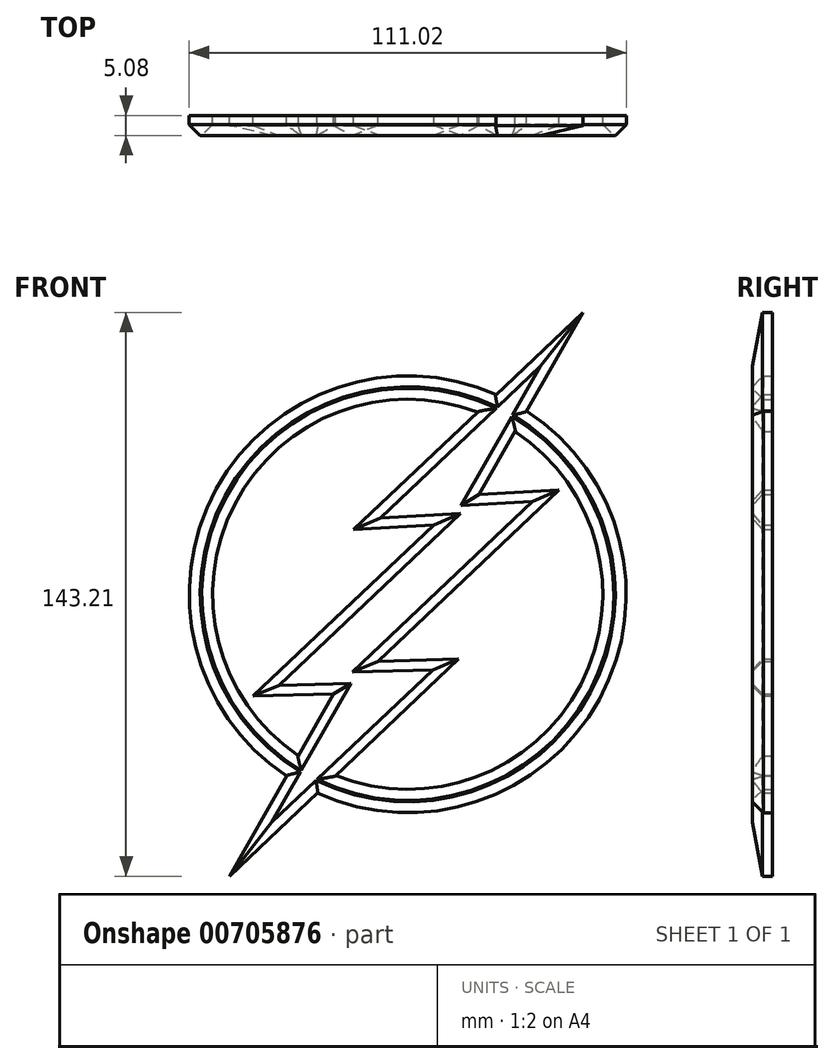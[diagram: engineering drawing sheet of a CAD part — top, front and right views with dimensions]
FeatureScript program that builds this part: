
annotation { "Feature Type Name" : "Feature", "Feature Type Description" : "" }
export const myFeature = defineFeature(function(context is Context, id is Id, definition is map)
    precondition{}
    {
        {
            var Q0;
            Q0=qCreatedBy(makeId("Front.planeOp"),FACE);
            var sketch = newSketch(context, id + "F0", { "sketchPlane" : qUnion([Q0])});
            skLineSegment(sketch, "E0", {"start": v(44.49, 71.6) * mm, "end": v(-13.73, 16.46) * mm});
            skLineSegment(sketch, "E1", {"start": v(38.43, 26.46) * mm, "end": v(18.04, 25.32) * mm});
            skLineSegment(sketch, "E2", {"start": v(18.04, 25.32) * mm, "end": v(44.49, 71.6) * mm});
            skLineSegment(sketch, "E3.MirrorCS", {"start": v(-45.3, -71.61) * mm, "end": v(12.92, -16.48) * mm});
            skLineSegment(sketch, "E4.MirrorCS", {"start": v(-39.27, -25.89) * mm, "end": v(-18.85, -25.33) * mm});
            skLineSegment(sketch, "E5", {"start": v(-18.85, -25.33) * mm, "end": v(-45.3, -71.61) * mm});
            skLineSegment(sketch, "E6", {"start": v(6.66, 17.61) * mm, "end": v(-39.27, -25.89) * mm});
            skLineSegment(sketch, "E7", {"start": v(-7.5, -17.03) * mm, "end": v(38.43, 26.46) * mm});
            skLineSegment(sketch, "E8", {"start": v(6.66, 17.61) * mm, "end": v(-13.73, 16.46) * mm});
            skLineSegment(sketch, "E9", {"start": v(12.92, -16.48) * mm, "end": v(-7.5, -17.03) * mm});
            skSolve(sketch);
        }
        {
            var Q0;
            Q0=qCreatedBy(makeId("Front.planeOp"),FACE);
            var sketch = newSketch(context, id + "F1", { "sketchPlane" : qUnion([Q0])});
            skCircle(sketch, "E10", {"center": v(0, 0) * mm, "radius": 55.5 * mm});
            skCircle(sketch, "E11", {"center": v(0, 0) * mm, "radius": 49.55 * mm});
            skSolve(sketch);
        }
        {
            var Q0;
            Q0=makeQuery(id+"F1.imprint","IMPRINT",FACE,{"disambiguationData":[TD([[makeQuery(id+"F1.imprint","IMPRINT",EDGE,{"derivedFrom":sQuery(id+"F1.wireOp",EDGE,"E10")}),1.0]])]});
            extrude(context, id + "F2", {"entities" : qUnion([Q0]), "depth" : 3.56 * mm, "offsetDistance" : 25.4 * mm});
        }
        {
            var Q0;
            Q0=makeQuery(id+"F2.opExtrude","CAP_EDGE",EDGE,{"disambiguationData":[OSD([sQuery(id+"F1.wireOp",EDGE,"E10")])],"isStart":false});
            var Q1;
            Q1=makeQuery(id+"F2.opExtrude","CAP_EDGE",EDGE,{"disambiguationData":[OSD([sQuery(id+"F1.wireOp",EDGE,"E11")])],"isStart":false});
            chamfer(context, id + "F3", {"entities" : qUnion([Q0, Q1]), "width" : 2.8 * mm, "tangentPropagation" : true});
        }
        {
            var Q0;
            Q0 = qSketchRegion(id + "F0", true);
            var Q1;
            Q1 = qSketchRegion(id + "F1", true);
            extrude(context, id + "F4", {"entities" : qUnion([Q0, Q1]), "operationType" : NewBodyOperationType.ADD, "depth" : 5.08 * mm, "offsetDistance" : 25.4 * mm});
        }
        {
            var Q0;
            Q0=makeQuery(id+"F4.opExtrude","CAP_EDGE",EDGE,{"disambiguationData":[OSD([sQuery(id+"F0.wireOp",EDGE,"E0")])],"isStart":false});
            var Q1;
            Q1=makeQuery(id+"F4.opExtrude","CAP_EDGE",EDGE,{"disambiguationData":[OSD([sQuery(id+"F0.wireOp",EDGE,"E2")])],"isStart":false});
            var Q2;
            Q2=makeQuery(id+"F4.opExtrude","CAP_EDGE",EDGE,{"disambiguationData":[OSD([sQuery(id+"F0.wireOp",EDGE,"E8")])],"isStart":false});
            var Q3;
            Q3=makeQuery(id+"F4.opExtrude","CAP_EDGE",EDGE,{"disambiguationData":[OSD([sQuery(id+"F0.wireOp",EDGE,"E6")])],"isStart":false});
            var Q4;
            Q4=makeQuery(id+"F4.opExtrude","CAP_EDGE",EDGE,{"disambiguationData":[OSD([sQuery(id+"F0.wireOp",EDGE,"E7")])],"isStart":false});
            var Q5;
            Q5=makeQuery(id+"F4.opExtrude","CAP_EDGE",EDGE,{"disambiguationData":[OSD([sQuery(id+"F0.wireOp",EDGE,"E1")])],"isStart":false});
            var Q6;
            Q6=makeQuery(id+"F4.opExtrude","CAP_EDGE",EDGE,{"disambiguationData":[OSD([sQuery(id+"F0.wireOp",EDGE,"E9")])],"isStart":false});
            var Q7;
            Q7=makeQuery(id+"F4.opExtrude","CAP_EDGE",EDGE,{"disambiguationData":[OSD([sQuery(id+"F0.wireOp",EDGE,"E4.MirrorCS")])],"isStart":false});
            var Q8;
            Q8=makeQuery(id+"F4.opExtrude","CAP_EDGE",EDGE,{"disambiguationData":[OSD([sQuery(id+"F0.wireOp",EDGE,"E3.MirrorCS")])],"isStart":false});
            var Q9;
            Q9=makeQuery(id+"F4.opExtrude","CAP_EDGE",EDGE,{"disambiguationData":[OSD([sQuery(id+"F0.wireOp",EDGE,"E5")])],"isStart":false});
            chamfer(context, id + "F5", {"entities" : qUnion([Q0, Q1, Q2, Q3, Q4, Q5, Q6, Q7, Q8, Q9]), "width" : 2.54 * mm, "tangentPropagation" : true});
        }
        {
            var Q0;
            {var subQ1=sQuery(id+"F0.wireOp",EDGE,"E0");var subQ2=sQuery(id+"F1.wireOp",EDGE,"E10");Q0=makeQuery(id+"F4.boolean.opBoolean","SPLIT",EDGE,{"disambiguationData":[TD([makeQuery(id+"F4.opExtrude","SWEPT_FACE",FACE,{"disambiguationData":[OSD([subQ1])]})])],"derivedFrom":makeQuery(id+"F4.opExtrude","CAP_EDGE",EDGE,{"disambiguationData":[OSD([subQ2])],"isStart":false})});}
            var Q1;
            {var subQ1=sQuery(id+"F0.wireOp",EDGE,"E0");var subQ2=sQuery(id+"F1.wireOp",EDGE,"E11");Q1=makeQuery(id+"F4.boolean.opBoolean","SPLIT",EDGE,{"disambiguationData":[TD([makeQuery(id+"F4.opExtrude","SWEPT_FACE",FACE,{"disambiguationData":[OSD([subQ1])]})])],"derivedFrom":makeQuery(id+"F4.opExtrude","CAP_EDGE",EDGE,{"disambiguationData":[OSD([subQ2])],"isStart":false})});}
            var Q2;
            {var subQ1=sQuery(id+"F0.wireOp",EDGE,"E2");var subQ2=sQuery(id+"F1.wireOp",EDGE,"E11");Q2=makeQuery(id+"F4.boolean.opBoolean","SPLIT",EDGE,{"disambiguationData":[TD([makeQuery(id+"F4.opExtrude","SWEPT_FACE",FACE,{"disambiguationData":[OSD([subQ1])]})])],"derivedFrom":makeQuery(id+"F4.opExtrude","CAP_EDGE",EDGE,{"disambiguationData":[OSD([subQ2])],"isStart":false})});}
            var Q3;
            {var subQ1=sQuery(id+"F0.wireOp",EDGE,"E2");var subQ2=sQuery(id+"F1.wireOp",EDGE,"E10");Q3=makeQuery(id+"F4.boolean.opBoolean","SPLIT",EDGE,{"disambiguationData":[TD([makeQuery(id+"F4.opExtrude","SWEPT_FACE",FACE,{"disambiguationData":[OSD([subQ1])]})])],"derivedFrom":makeQuery(id+"F4.opExtrude","CAP_EDGE",EDGE,{"disambiguationData":[OSD([subQ2])],"isStart":false})});}
            chamfer(context, id + "F6", {"entities" : qUnion([Q0, Q1, Q2, Q3]), "width" : 2.8 * mm, "tangentPropagation" : true});
        }
    });
